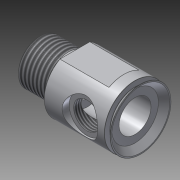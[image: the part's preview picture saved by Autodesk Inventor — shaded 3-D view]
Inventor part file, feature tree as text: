
AUTODESK INVENTOR PART (.ipt)
format: ipt  version: 2014 SP1 (Build 180222100, 222)  size: 238,592 bytes
history: native  units: in
note: dims shown in document units (in); Inventor stores cm internally (conversion verified against a paired STEP export)
features: extrude x3, sketch x2, thread x2, chamfer x2, revolve x1, pattern_circular x1, fillet x1, plane x1
ambient origin geometry x8: Origin, YZ Plane, XZ Plane, XY Plane, X Axis, Y Axis, Z Axis, Center Point
bodies: Solid1 (feature_tree)
feature tree (13):
  sketch  "Sketch1"  dims[d0=0.6875in d2=0.624in]
  revolve  "Revolution1"  [1 undecoded]
  extrude  "Extrusion1"  Depth=0.002in
  extrude  "Extrusion2"  Depth=0.002in
  thread  "Thread1"  [1 undecoded]
  chamfer  "Chamfer1"  Distance=0.75in
  chamfer  "Chamfer2"  Distance=0.86in
  pattern_circular  "Circular Pattern1"  [2 undecoded]
  thread  "Thread3"  [1 undecoded]
  fillet  "Fillet1"  Radius=1.425in
  plane  "Work Plane1"
  extrude  "Extrusion4"  TaperAngle=90.0deg  [1 undecoded]
  sketch  "Sketch2"  dims[d3=0.625in d4=0.09in d5=0.5in d6=0.25in d7=0.75in d8=0.86in d9=0.7in d10=45.0deg d11=1.425in d12=90.0deg d13=1.0in d14=0.0in d15=0.02in d16=0.125in d17=45.0deg d18=1.0in d19=0.0in d20=0.7874in d21=360.0deg d23=0.375in d24=1.0in d25=0.25in d26=0.0in d29=0.03in d30=0.125in d31=45.0deg d32=0.392in d33=0.0in d34=0.45in d35=0.75in d36=0.015in d37=0.002in d41=0.5in d42=0.1in d43=0.0in d44=0.1898in d45=0.475in d46=0.35in]
note: 6 required parameter values undecoded (feature->parameter linkage not recoverable at this tier; creation-order binding heuristic only, values carry confidence <= 0.55)